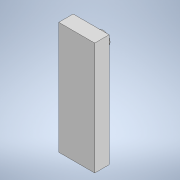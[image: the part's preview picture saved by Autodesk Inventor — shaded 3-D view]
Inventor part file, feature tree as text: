
AUTODESK INVENTOR PART (.ipt)
format: ipt  version: 2021.2 (Build 252289000, 289)  size: 115,712 bytes
history: native  units: in
note: dims shown in document units (in); Inventor stores cm internally (conversion verified against a paired STEP export)
features: extrude x4, sketch x3
ambient origin geometry x8: Origin, YZ Plane, XZ Plane, XY Plane, X Axis, Y Axis, Z Axis, Center Point
bodies: Solid1 (feature_tree)
feature tree (7):
  extrude  "Extrusion1"  Depth=3.0in
  extrude  "Extrusion3"  Depth=0.4in TaperAngle=0.0deg
  sketch  "Sketch4"  dims[d9=0.15in d10=0.38in d11=0.275in d12=0.0in d13=0.3375in d14=0.0in]
  extrude  "Extrusion4"  Depth=0.3375in
  extrude  "Extrusion5"  Depth=0.275in TaperAngle=0.0deg
  sketch  "Sketch1"  dims[d0=1.0in d1=3.0in]
  sketch  "Sketch3"  dims[d2=0.4in d3=0.0in d6=0.13in d7=0.0in]
